# Revit family: IS_Conca_T4318_BIM_IT
name_source: partatom
category: Plumbing Fixtures
revit_build: Autodesk Revit 2017 (Build: 20160225_1515(x64)
units: mm (PartAtom-declared; Revit-internal decimal feet)

## family parameters
Always vertical = No
Cut with Voids When Loaded = No
OmniClass Number = 23.45.05.14.21.11
OmniClass Title = Bath/Shower Units
Part Type = Normal
Room Calculation Point = No
Round Connector Dimension = Use Diameter
Shared = No
Work Plane-Based = No

## types (6) — shared parameters
Accessori = https://www.idealstandard.it
Aiuto = https://www.idealstandard.it
AltezzaNominale = 550 mm
Autore = Ideal Standard
BIMobject category = Storage
BIMobject category code = sanitary-storage
BIMobject main category = Sanitary
BIMobject main category code = sanitary
Brand = https://www.idealstandard.it
DescrizioneClassifcazioneUni2015 = Bathroom cabinets
DurataGaranzia = 2
DurataGaranziaProdotti = 2
Forma = Rettangolare
Garanzia = Garanzia Idealstandard
IfcEsportaCome = IfcFurnitureType
InformaziniGaranzia = https://www.idealstandard.it
InformazioniDiProdotto = http://www.idealstandard.it
InformazioniGaranzia = https://www.idealstandard.it
Installation instructions = https://www.idealspec.co.uk
InstruzioniInstallazione = https://www.idealstandard.it
LarghezzaNominale = 802 mm  [stored 2.63123 ft]
Maniglia = No
Manufacturer = Ideal Standard
Materiale = Ceramics
NettWeight = 35.2
NominalDepth = 373 mm  [stored 1.22375 ft]
NominalHeight = 550 mm
NominalWidth = 802 mm  [stored 2.63123 ft]
PesoNetto = 35.2
PiattoDoccia = No
Product group = Bathroom_Furniture
Produttore = Ideal Standard
ProfonditaNominale = 373 mm  [stored 1.22375 ft]
Revisione = 1
RiferimentoClassificazioneUni2015 = Pr_40_30_78_03
Spazio = Interno
Telefono = 800 652 290
TipoEspotazioneIfc = Bathroom cabinets
URL = https://www.ideal-standard.co.uk
Uniclass 2015 Code = Pr_40_30_78_03
Uniclass 2015 Name = Bathroom cabinets
UnitàDurata = Anno
UnitàDurataGaranzia = Anno
UnitàLineare = Milimitre
UnitàMonetaria = €
UnitàSuperficie = Milimitre
UnitàVolume = Litri
Versione = 1
VersioneClassificazioneUni2015 = v1.1
zero-valued in all types: CostoDiSostituzione, DimensioneScarico, LunghezzaNominale, Nominal depth, Nominal height, NominalLength, SeatMaterial, SpessoreDelMateriale, SpilloverLivello, Weight Net (Kg)

## per-type parameters (varying)
| type | Caratteristiche | CodiceABarre | CodiceArticolo | Colore | Description | Desrizione | Finitura | Model | ModelNumber | ModelloDiRiferimento | Nome | NomeOggettoBim | NumeroDiModello |
| T4318Y1 - BSN UN 80X37X55 1 DR+WTOP NOCUT  WHMT | Mobile sottolavabo, 800 x 372 x 550mm con piano da appoggio non forato, 1 cassetto interno ed 1 cassetto esterno. Dotato di tecnologia push open e soft close. Cassetti in metallo.Finitura Bianco laccato opaco. | 8014140463795 | T4318Y1 | Matt white | Vanity unit, 800 x 372 x 550mm with non-perforated countertop, 1 internal drawer and 1 external drawer. Equipped with push open and soft close technology.  Matt white lacquered finish. | Mobile sottolavabo, 800 x 372 x 550mm con piano da appoggio non forato, 1 cassetto interno ed 1 cassetto esterno. Dotato di tecnologia push open e soft close. Cassetti in metallo.Finitura Bianco laccato opaco. | Matt white | T4318Y1 | T4318Y1 | T4318Y1 | BathroomCabinets_Conca_T4318Y1_IdealStandard | ISI_IdealStandard_Bathroom Cabinets_Conca_T4318Y1 | T4318Y1 |
| T4318Y2 - BSN UN 80X37X55 1 DR+WTOP NOCUT  ANMT | Mobile sottolavabo, 800 x 372 x 550mm con piano da appoggio non forato, 1 cassetto interno ed 1 cassetto esterno. Dotato di tecnologia push open e soft close. Cassetti in metallo.Finitura Antracite laccato opaco. | 8014140463801 | T4318Y2 | Matt anthracite | Vanity unit, 800 x 372 x 550mm with non-perforated countertop, 1 internal drawer and 1 external drawer. Equipped with push open and soft close technology.  Anthracite matt lacquer finish. | Mobile sottolavabo, 800 x 372 x 550mm con piano da appoggio non forato, 1 cassetto interno ed 1 cassetto esterno. Dotato di tecnologia push open e soft close. Cassetti in metallo.Finitura Antracite laccato opaco. | Matt anthracite | T4318Y2 | T4318Y2 | T4318Y2 | BathroomCabinets_Conca_T4318Y2_IdealStandard | ISI_IdealStandard_Bathroom Cabinets_Conca_T4318Y2 | T4318Y2 |
| T4318Y3 - BSN UN 80X37X55 1 DR+WTOP NOCUT   SNMT | Mobile sottolavabo, 800 x 372 x 550mm con piano da appoggio non forato, 1 cassetto interno ed 1 cassetto esterno. Dotato di tecnologia push open e soft close. Cassetti in metallo.Finitura Sunset laccato opaco. | 8014140463818 | T4318Y3 | Matt Sunset | Vanity unit, 800 x 372 x 550mm with non-perforated countertop, 1 internal drawer and 1 external drawer. Equipped with push open and soft close technology.  Sunset matt lacquer finish. | Mobile sottolavabo, 800 x 372 x 550mm con piano da appoggio non forato, 1 cassetto interno ed 1 cassetto esterno. Dotato di tecnologia push open e soft close. Cassetti in metallo.Finitura Sunset laccato opaco. | Matt Sunset | T4318Y3 | T4318Y3 | T4318Y3 | BathroomCabinets_Conca_T4318Y3_IdealStandard | ISI_IdealStandard_Bathroom Cabinets_Conca_T4318Y3 | T4318Y3 |
| T4318Y4 - BSN UN 80X37X55 1 DR+WTOP  NOCUT   SMOK | Mobile sottolavabo, 800 x 372 x 550mm con piano da appoggio non forato, 1 cassetto interno ed 1 cassetto esterno. Dotato di tecnologia push open e soft close. Cassetti in metallo.Finitura Rovere affumicato scuro. | 8014140463825 | T4318Y4 | Smoked Oak | Vanity unit, 800 x 372 x 550mm with non-perforated countertop, 1 internal drawer and 1 external drawer. Equipped with push open and soft close technology.  Dark smoked oak finish. | Mobile sottolavabo, 800 x 372 x 550mm con piano da appoggio non forato, 1 cassetto interno ed 1 cassetto esterno. Dotato di tecnologia push open e soft close. Cassetti in metallo.Finitura Rovere affumicato scuro. | Smoked Oak | T4318Y4 | T4318Y4 | T4318Y4 | BathroomCabinets_Conca_T4318Y4_IdealStandard | ISI_IdealStandard_Bathroom Cabinets_Conca_T4318Y4 | T4318Y4 |
| T4318Y5 - BSN UN 80X37X55 1 DR+WTOP NOCUT DKWN | Mobile sottolavabo, 800 x 372 x 550mm con piano da appoggio non forato, 1 cassetto interno ed 1 cassetto esterno. Dotato di tecnologia push open e soft close. Cassetti in metallo.Finitura Noce scuro. | 8014140463832 | T4318Y5 | Dark Walnut | Vanity unit, 800 x 372 x 550mm with non-perforated countertop, 1 internal drawer and 1 external drawer. Equipped with push open and soft close technology.  Dark Walnut finish. | Mobile sottolavabo, 800 x 372 x 550mm con piano da appoggio non forato, 1 cassetto interno ed 1 cassetto esterno. Dotato di tecnologia push open e soft close. Cassetti in metallo.Finitura Noce scuro. | Dark Walnut | T4318Y5 | T4318Y5 | T4318Y5 | BathroomCabinets_Conca_T4318Y5_IdealStandard | ISI_IdealStandard_Bathroom Cabinets_Conca_T4318Y5 | T4318Y5 |
| T4318Y6 - BSN UN 80X37X55 1 DR+WTOP NOCUT   LTOK | Mobile sottolavabo, 800 x 372 x 550mm con piano da appoggio non forato, 1 cassetto interno ed 1 cassetto esterno. Dotato di tecnologia push open e soft close. Cassetti in metallo.Finitura Legno chiaro. | 8014140463849 | T4318Y6 | Light Oak | Vanity unit, 800 x 372 x 550mm with non-perforated countertop, 1 internal drawer and 1 external drawer. Equipped with push open and soft close technology.  Light wood finish. | Mobile sottolavabo, 800 x 372 x 550mm con piano da appoggio non forato, 1 cassetto interno ed 1 cassetto esterno. Dotato di tecnologia push open e soft close. Cassetti in metallo.Finitura Legno chiaro. | Light Oak | T4318Y6 | T4318Y6 | T4318Y6 | BathroomCabinets_Conca_T4318Y6_IdealStandard | ISI_IdealStandard_Bathroom Cabinets_Conca_T4318Y6 | T4318Y6 |

note: [stored X ft] marks values corroborated as IEEE doubles in the binary element streams (Revit-internal decimal feet)

## geometry (parser evidence)
native form markers: Sweep x4
no freeform markers — native parametric forms only
